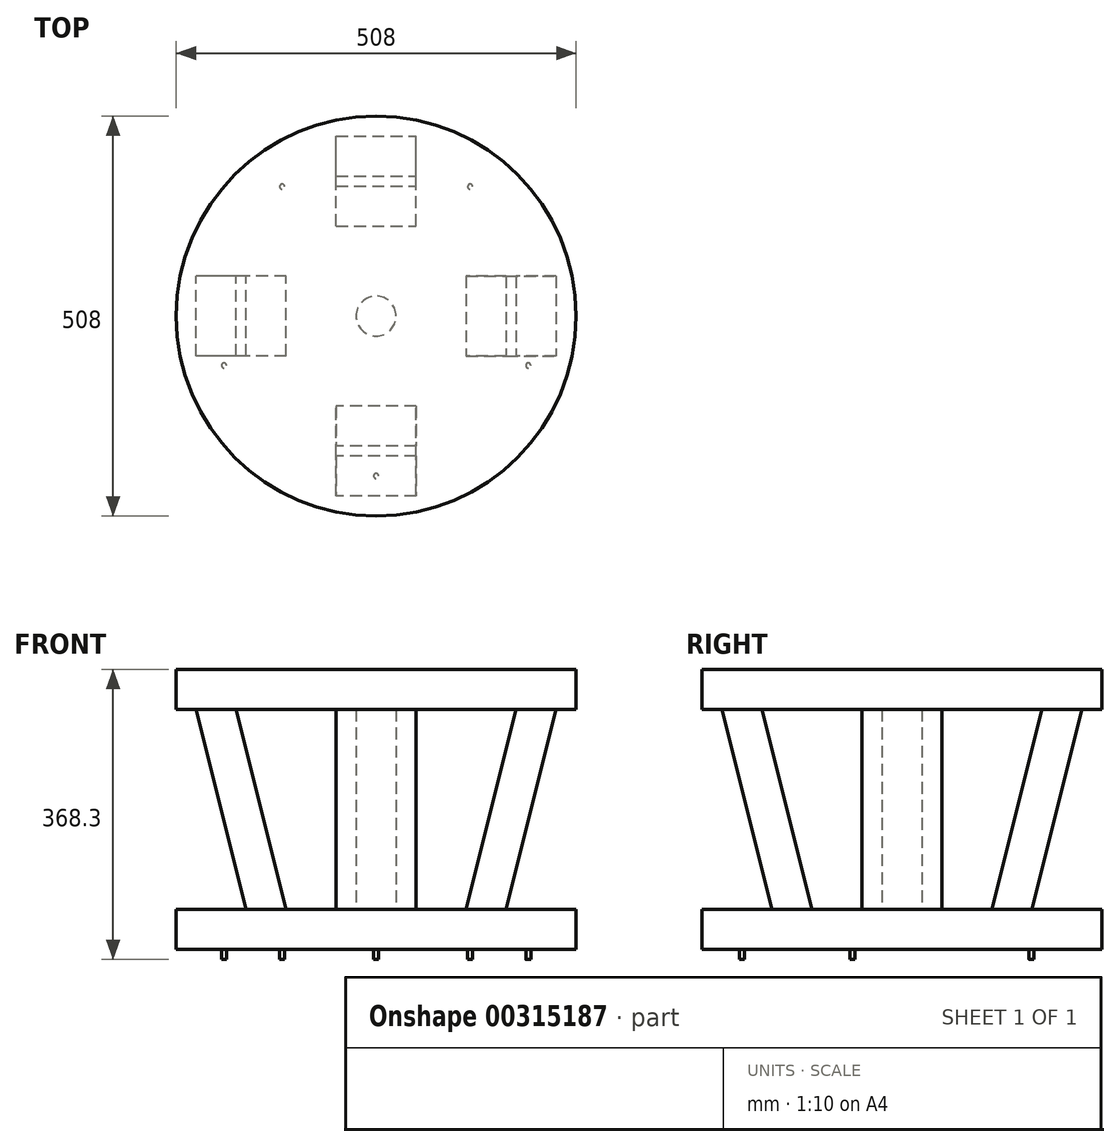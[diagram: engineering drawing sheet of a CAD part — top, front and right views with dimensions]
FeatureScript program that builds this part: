
annotation { "Feature Type Name" : "Feature", "Feature Type Description" : "" }
export const myFeature = defineFeature(function(context is Context, id is Id, definition is map)
    precondition{}
    {
        {
            var Q0;
            Q0=qCreatedBy(makeId("Top.planeOp"),FACE);
            var sketch = newSketch(context, id + "F0", { "sketchPlane" : qUnion([Q0])});
            skCircle(sketch, "E0", {"center": v(0, 0) * mm, "radius": 254 * mm});
            skSolve(sketch);
        }
        {
            var Q0;
            Q0=makeQuery(id+"F0.imprint","IMPRINT",FACE,{"disambiguationData":[TD([[makeQuery(id+"F0.imprint","IMPRINT",EDGE,{"derivedFrom":sQuery(id+"F0.wireOp",EDGE,"E0")}),1.0]])]});
            extrude(context, id + "F1", {"entities" : qUnion([Q0]), "depth" : 50.8 * mm});
        }
        {
            var Q0;
            Q0=makeQuery(id+"F1.opExtrude","CAP_FACE",FACE,{"disambiguationData":[OSD([sQuery(id+"F0.wireOp",EDGE,"E0")])],"isStart":false});
            var sketch = newSketch(context, id + "F2", { "sketchPlane" : qUnion([Q0])});
            skCircle(sketch, "E1", {"center": v(0, 0) * mm, "radius": 25.4 * mm});
            skSolve(sketch);
        }
        {
            var Q0;
            Q0=makeQuery(id+"F2.imprint","IMPRINT",FACE,{"disambiguationData":[TD([[makeQuery(id+"F2.imprint","IMPRINT",EDGE,{"derivedFrom":sQuery(id+"F2.wireOp",EDGE,"E1")}),1.0]])]});
            extrude(context, id + "F3", {"entities" : qUnion([Q0]), "operationType" : NewBodyOperationType.ADD, "depth" : 254 * mm});
        }
        {
            var Q0;
            Q0=makeQuery(id+"F1.opExtrude","CAP_FACE",FACE,{"disambiguationData":[OSD([sQuery(id+"F0.wireOp",EDGE,"E0")])],"isStart":false});
            var sketch = newSketch(context, id + "F4", { "sketchPlane" : qUnion([Q0])});
            skLineSegment(sketch, "E2.bottom", {"start": v(-114.3, -50.8) * mm, "end": v(-165.1, -50.8) * mm});
            skLineSegment(sketch, "E2.top", {"start": v(-114.3, 50.8) * mm, "end": v(-165.1, 50.8) * mm});
            skLineSegment(sketch, "E2.left", {"start": v(-114.3, -50.8) * mm, "end": v(-114.3, 50.8) * mm});
            skLineSegment(sketch, "E2.right", {"start": v(-165.1, -50.8) * mm, "end": v(-165.1, 50.8) * mm});
            skPoint(sketch, "E2.middle", {"position": v(-139.7, 0) * mm});
            skSolve(sketch);
        }
        {
            var Q0;
            Q0=makeQuery(id+"F1.opExtrude","CAP_FACE",FACE,{"disambiguationData":[OSD([sQuery(id+"F0.wireOp",EDGE,"E0")])],"isStart":false});
            var sketch = newSketch(context, id + "F5", { "sketchPlane" : qUnion([Q0])});
            skLineSegment(sketch, "E3.bottom", {"start": v(-50.8, 114.3) * mm, "end": v(50.8, 114.3) * mm});
            skLineSegment(sketch, "E3.top", {"start": v(-50.8, 165.1) * mm, "end": v(50.8, 165.1) * mm});
            skLineSegment(sketch, "E3.left", {"start": v(-50.8, 114.3) * mm, "end": v(-50.8, 165.1) * mm});
            skLineSegment(sketch, "E3.right", {"start": v(50.8, 114.3) * mm, "end": v(50.8, 165.1) * mm});
            skPoint(sketch, "E3.middle", {"position": v(0, 139.7) * mm});
            skSolve(sketch);
        }
        {
            var Q0;
            Q0=makeQuery(id+"F1.opExtrude","CAP_FACE",FACE,{"disambiguationData":[OSD([sQuery(id+"F0.wireOp",EDGE,"E0")])],"isStart":false});
            var sketch = newSketch(context, id + "F6", { "sketchPlane" : qUnion([Q0])});
            skLineSegment(sketch, "E4.bottom", {"start": v(165.1, 50.8) * mm, "end": v(114.3, 50.8) * mm});
            skLineSegment(sketch, "E4.top", {"start": v(165.1, -50.8) * mm, "end": v(114.3, -50.8) * mm});
            skLineSegment(sketch, "E4.left", {"start": v(165.1, 50.8) * mm, "end": v(165.1, -50.8) * mm});
            skLineSegment(sketch, "E4.right", {"start": v(114.3, 50.8) * mm, "end": v(114.3, -50.8) * mm});
            skPoint(sketch, "E4.middle", {"position": v(139.7, 0) * mm});
            skLineSegment(sketch, "E5.bottom", {"start": v(-50.8, -165.1) * mm, "end": v(50.8, -165.1) * mm});
            skLineSegment(sketch, "E5.top", {"start": v(-50.8, -114.3) * mm, "end": v(50.8, -114.3) * mm});
            skLineSegment(sketch, "E5.left", {"start": v(-50.8, -165.1) * mm, "end": v(-50.8, -114.3) * mm});
            skLineSegment(sketch, "E5.right", {"start": v(50.8, -165.1) * mm, "end": v(50.8, -114.3) * mm});
            skPoint(sketch, "E5.middle", {"position": v(0, -139.7) * mm});
            skSolve(sketch);
        }
        {
            var Q0;
            Q0=makeQuery(id+"F3.opExtrude","CAP_FACE",FACE,{"disambiguationData":[OSD([sQuery(id+"F2.wireOp",EDGE,"E1")])],"isStart":false});
            var sketch = newSketch(context, id + "F7", { "sketchPlane" : qUnion([Q0])});
            skCircle(sketch, "E6", {"center": v(0, 0) * mm, "radius": 254 * mm});
            skSolve(sketch);
        }
        {
            var Q0;
            Q0 = qSketchRegion(id + "F7", true);
            extrude(context, id + "F8", {"entities" : qUnion([Q0]), "operationType" : NewBodyOperationType.ADD, "depth" : 50.8 * mm});
        }
        {
            var Q0;
            Q0=makeQuery(id+"F8.opExtrude","CAP_FACE",FACE,{"disambiguationData":[OSD([sQuery(id+"F7.wireOp",EDGE,"E6")])],"isStart":true});
            var sketch = newSketch(context, id + "F9", { "sketchPlane" : qUnion([Q0])});
            skLineSegment(sketch, "E7.bottom", {"start": v(50.8, 177.8) * mm, "end": v(-50.8, 177.8) * mm});
            skLineSegment(sketch, "E7.top", {"start": v(50.8, 228.6) * mm, "end": v(-50.8, 228.6) * mm});
            skLineSegment(sketch, "E7.left", {"start": v(50.8, 177.8) * mm, "end": v(50.8, 228.6) * mm});
            skLineSegment(sketch, "E7.right", {"start": v(-50.8, 177.8) * mm, "end": v(-50.8, 228.6) * mm});
            skPoint(sketch, "E7.middle", {"position": v(0, 203.2) * mm});
            skLineSegment(sketch, "E8.bottom", {"start": v(177.8, 50.8) * mm, "end": v(228.6, 50.8) * mm});
            skLineSegment(sketch, "E8.top", {"start": v(177.8, -50.8) * mm, "end": v(228.6, -50.8) * mm});
            skLineSegment(sketch, "E8.left", {"start": v(177.8, 50.8) * mm, "end": v(177.8, -50.8) * mm});
            skLineSegment(sketch, "E8.right", {"start": v(228.6, 50.8) * mm, "end": v(228.6, -50.8) * mm});
            skPoint(sketch, "E8.middle", {"position": v(203.2, 0) * mm});
            skLineSegment(sketch, "E9.bottom", {"start": v(50.8, -228.6) * mm, "end": v(-50.8, -228.6) * mm});
            skLineSegment(sketch, "E9.top", {"start": v(50.8, -177.8) * mm, "end": v(-50.8, -177.8) * mm});
            skLineSegment(sketch, "E9.left", {"start": v(50.8, -228.6) * mm, "end": v(50.8, -177.8) * mm});
            skLineSegment(sketch, "E9.right", {"start": v(-50.8, -228.6) * mm, "end": v(-50.8, -177.8) * mm});
            skPoint(sketch, "E9.middle", {"position": v(0, -203.2) * mm});
            skLineSegment(sketch, "E10.bottom", {"start": v(-177.8, -50.8) * mm, "end": v(-228.6, -50.8) * mm});
            skLineSegment(sketch, "E10.top", {"start": v(-177.8, 50.8) * mm, "end": v(-228.6, 50.8) * mm});
            skLineSegment(sketch, "E10.left", {"start": v(-177.8, -50.8) * mm, "end": v(-177.8, 50.8) * mm});
            skLineSegment(sketch, "E10.right", {"start": v(-228.6, -50.8) * mm, "end": v(-228.6, 50.8) * mm});
            skPoint(sketch, "E10.middle", {"position": v(-203.2, 0) * mm});
            skSolve(sketch);
        }
        {
            var Q0;
            Q0=qCreatedBy(makeId("Right.planeOp"),FACE);
            var sketch = newSketch(context, id + "F10", { "sketchPlane" : qUnion([Q0])});
            skLineSegment(sketch, "E11", {"start": v(-139.7, 50.8) * mm, "end": v(-203.2, 304.8) * mm});
            skSolve(sketch);
        }
        {
            var Q0;
            Q0=makeQuery(id+"F9.imprint","IMPRINT",FACE,{"disambiguationData":[TD([[makeQuery(id+"F9.imprint","IMPRINT",EDGE,{"derivedFrom":sQuery(id+"F9.wireOp",EDGE,"E7.bottom")}),-1.0]])]});
            var Q1;
            Q1=makeQuery(id+"F6.imprint","IMPRINT",FACE,{"disambiguationData":[TD([[makeQuery(id+"F6.imprint","IMPRINT",EDGE,{"derivedFrom":sQuery(id+"F6.wireOp",EDGE,"E5.bottom")}),1.0]])]});
            var Q2;
            Q2=sQuery(id+"F10.wireOp",EDGE,"E11");
            sweep(context, id + "F11", {"profiles" : qUnion([Q0, Q1]), "path" : qUnion([Q2])});
        }
        {
            var Q0;
            Q0=makeQuery(id+"F11.opSweep","SWEPT_BODY",BODY,{"disambiguationData":[OSD([sQuery(id+"F6.wireOp",EDGE,"E5.bottom"),sQuery(id+"F6.wireOp",EDGE,"E5.top"),sQuery(id+"F6.wireOp",EDGE,"E5.left"),sQuery(id+"F6.wireOp",EDGE,"E5.right"),sQuery(id+"F10.wireOp",EDGE,"E11")])]});
            deleteBodies(context, id + "F12", {"entities" : qUnion([Q0])});
        }
        {
            var Q0;
            Q0=qCreatedBy(makeId("Front.planeOp"),FACE);
            var sketch = newSketch(context, id + "F13", { "sketchPlane" : qUnion([Q0])});
            skLineSegment(sketch, "E12", {"start": v(139.7, 50.8) * mm, "end": v(203.2, 304.8) * mm});
            skSolve(sketch);
        }
        {
            var Q0;
            Q0=makeQuery(id+"F6.imprint","IMPRINT",FACE,{"disambiguationData":[TD([[makeQuery(id+"F6.imprint","IMPRINT",EDGE,{"derivedFrom":sQuery(id+"F6.wireOp",EDGE,"E4.bottom")}),1.0]])]});
            var Q1;
            Q1=makeQuery(id+"F9.imprint","IMPRINT",FACE,{"disambiguationData":[TD([[makeQuery(id+"F9.imprint","IMPRINT",EDGE,{"derivedFrom":sQuery(id+"F9.wireOp",EDGE,"E8.bottom")}),-1.0]])]});
            var Q2;
            Q2=sQuery(id+"F13.wireOp",EDGE,"E12");
            sweep(context, id + "F14", {"profiles" : qUnion([Q0, Q1]), "path" : qUnion([Q2])});
        }
        {
            var Q0;
            Q0=makeQuery(id+"F14.opSweep","SWEPT_BODY",BODY,{"disambiguationData":[OSD([sQuery(id+"F9.wireOp",EDGE,"E8.bottom"),sQuery(id+"F9.wireOp",EDGE,"E8.top"),sQuery(id+"F9.wireOp",EDGE,"E8.left"),sQuery(id+"F9.wireOp",EDGE,"E8.right"),sQuery(id+"F13.wireOp",EDGE,"E12")])]});
            deleteBodies(context, id + "F15", {"entities" : qUnion([Q0])});
        }
        {
            var Q0;
            Q0=qCreatedBy(makeId("Front.planeOp"),FACE);
            var sketch = newSketch(context, id + "F16", { "sketchPlane" : qUnion([Q0])});
            skLineSegment(sketch, "E13", {"start": v(-139.7, 50.8) * mm, "end": v(-203.2, 304.8) * mm});
            skSolve(sketch);
        }
        {
            var Q0;
            Q0=makeQuery(id+"F4.imprint","IMPRINT",FACE,{"disambiguationData":[TD([[makeQuery(id+"F4.imprint","IMPRINT",EDGE,{"derivedFrom":sQuery(id+"F4.wireOp",EDGE,"E2.bottom")}),-1.0]])]});
            var Q1;
            Q1=makeQuery(id+"F9.imprint","IMPRINT",FACE,{"disambiguationData":[TD([[makeQuery(id+"F9.imprint","IMPRINT",EDGE,{"derivedFrom":sQuery(id+"F9.wireOp",EDGE,"E10.bottom")}),-1.0]])]});
            var Q2;
            Q2=sQuery(id+"F16.wireOp",EDGE,"E13");
            sweep(context, id + "F17", {"profiles" : qUnion([Q0, Q1]), "path" : qUnion([Q2])});
        }
        {
            var Q0;
            Q0=makeQuery(id+"F17.opSweep","SWEPT_BODY",BODY,{"disambiguationData":[OSD([sQuery(id+"F9.wireOp",EDGE,"E10.bottom"),sQuery(id+"F9.wireOp",EDGE,"E10.top"),sQuery(id+"F9.wireOp",EDGE,"E10.left"),sQuery(id+"F9.wireOp",EDGE,"E10.right"),sQuery(id+"F16.wireOp",EDGE,"E13")])]});
            deleteBodies(context, id + "F18", {"entities" : qUnion([Q0])});
        }
        {
            var Q0;
            Q0=qCreatedBy(makeId("Right.planeOp"),FACE);
            var sketch = newSketch(context, id + "F19", { "sketchPlane" : qUnion([Q0])});
            skLineSegment(sketch, "E14", {"start": v(139.7, 50.8) * mm, "end": v(203.2, 304.8) * mm});
            skSolve(sketch);
        }
        {
            var Q0;
            Q0=makeQuery(id+"F5.imprint","IMPRINT",FACE,{"disambiguationData":[TD([[makeQuery(id+"F5.imprint","IMPRINT",EDGE,{"derivedFrom":sQuery(id+"F5.wireOp",EDGE,"E3.bottom")}),1.0]])]});
            var Q1;
            Q1=makeQuery(id+"F9.imprint","IMPRINT",FACE,{"disambiguationData":[TD([[makeQuery(id+"F9.imprint","IMPRINT",EDGE,{"derivedFrom":sQuery(id+"F9.wireOp",EDGE,"E9.bottom")}),-1.0]])]});
            var Q2;
            Q2=sQuery(id+"F19.wireOp",EDGE,"E14");
            sweep(context, id + "F20", {"profiles" : qUnion([Q0, Q1]), "path" : qUnion([Q2])});
        }
        {
            var Q0;
            Q0=makeQuery(id+"F20.opSweep","SWEPT_BODY",BODY,{"disambiguationData":[OSD([sQuery(id+"F9.wireOp",EDGE,"E9.bottom"),sQuery(id+"F9.wireOp",EDGE,"E9.top"),sQuery(id+"F9.wireOp",EDGE,"E9.left"),sQuery(id+"F9.wireOp",EDGE,"E9.right"),sQuery(id+"F19.wireOp",EDGE,"E14")])]});
            deleteBodies(context, id + "F21", {"entities" : qUnion([Q0])});
        }
        {
            var Q0;
            Q0=makeQuery(id+"F1.opExtrude","CAP_FACE",FACE,{"disambiguationData":[OSD([sQuery(id+"F0.wireOp",EDGE,"E0")])],"isStart":true});
            var sketch = newSketch(context, id + "F22", { "sketchPlane" : qUnion([Q0])});
            skCircle(sketch, "E15", {"center": v(0, 203.2) * mm, "radius": 3.18 * mm});
            skSolve(sketch);
        }
        {
            var Q0;
            Q0 = qSketchRegion(id + "F22", true);
            extrude(context, id + "F23", {"entities" : qUnion([Q0]), "operationType" : NewBodyOperationType.ADD, "depth" : 12.7 * mm});
        }
        {
            var Q0;
            Q0=makeQuery(id+"F1.opExtrude","SWEPT_BODY",BODY,{"disambiguationData":[OSD([sQuery(id+"F0.wireOp",EDGE,"E0")])]});
            var Q1;
            Q1=makeQuery(id+"F3.opExtrude","SWEPT_FACE",FACE,{"disambiguationData":[OSD([sQuery(id+"F2.wireOp",EDGE,"E1")])]});
            circularPattern(context, id + "F24", {"entities" : qUnion([Q0]), "axis" : qUnion([Q1]), "angle" : 360 * degree, "instanceCount" : 5, "equalSpace" : true});
        }
    });
